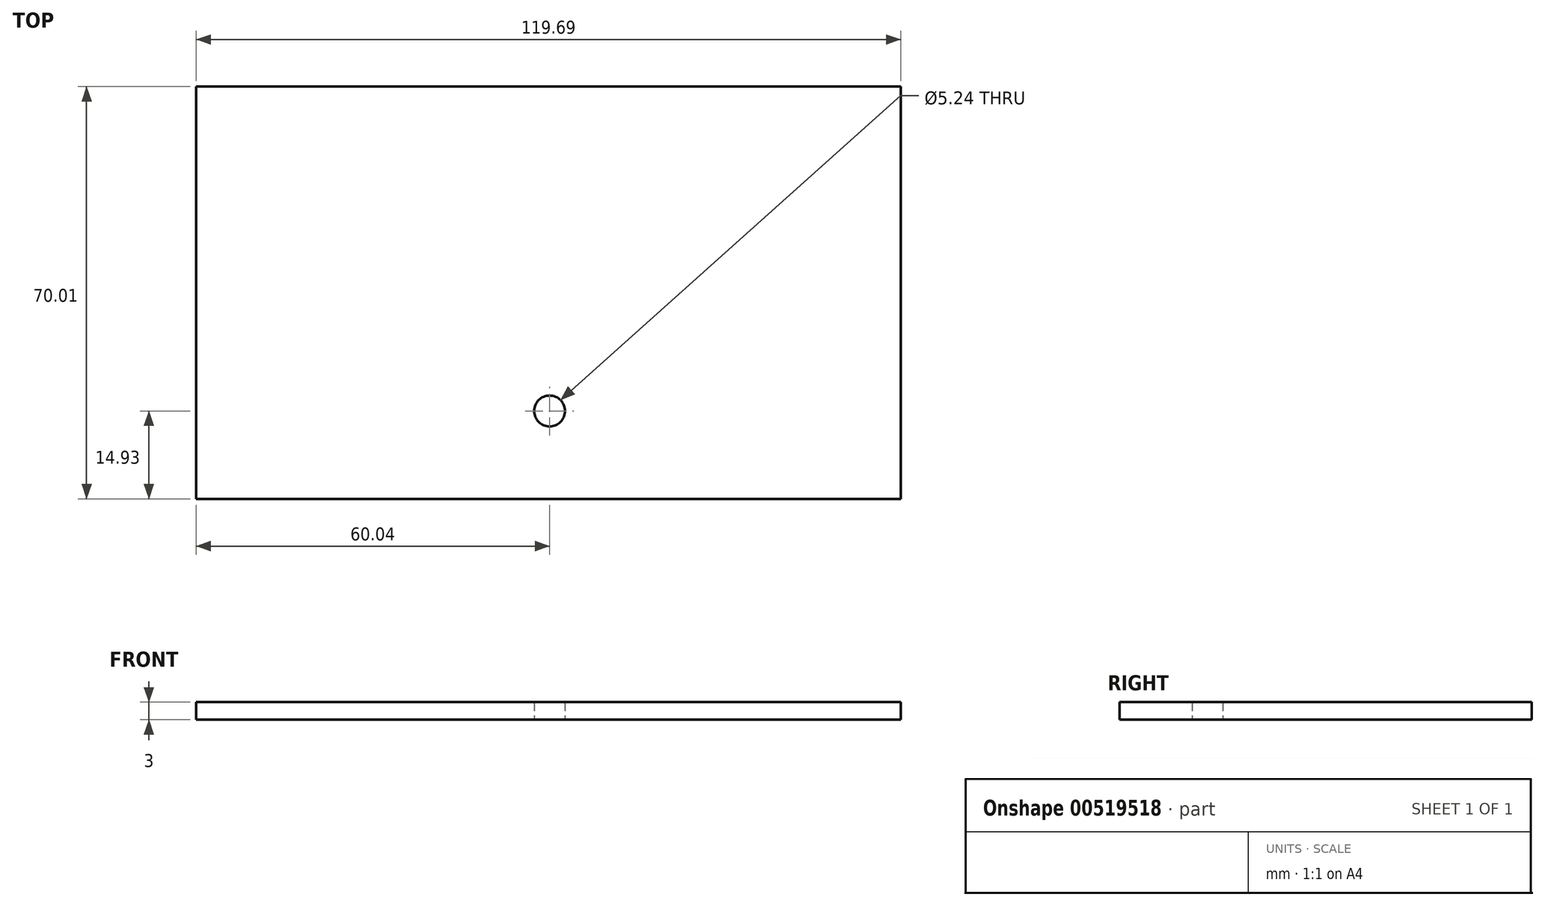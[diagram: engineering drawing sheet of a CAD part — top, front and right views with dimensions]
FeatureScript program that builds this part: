
annotation { "Feature Type Name" : "Feature", "Feature Type Description" : "" }
export const myFeature = defineFeature(function(context is Context, id is Id, definition is map)
    precondition{}
    {
        {
            var Q0;
            Q0=qCreatedBy(makeId("Top.planeOp"),FACE);
            var sketch = newSketch(context, id + "F0", { "sketchPlane" : qUnion([Q0])});
            skCircle(sketch, "E0", {"center": v(0, 0) * mm, "radius": 2.62 * mm});
            skLineSegment(sketch, "E1", {"start": v(0, -14.93) * mm, "end": v(59.65, -14.93) * mm});
            skLineSegment(sketch, "E2", {"start": v(59.65, -14.93) * mm, "end": v(59.65, 55.08) * mm});
            skLineSegment(sketch, "E3", {"start": v(59.65, 55.08) * mm, "end": v(-60.04, 55.08) * mm});
            skLineSegment(sketch, "E4", {"start": v(-60.04, 55.08) * mm, "end": v(-60.04, -14.93) * mm});
            skLineSegment(sketch, "E5", {"start": v(-60.04, -14.93) * mm, "end": v(0, -14.93) * mm});
            skSolve(sketch);
        }
        {
            var Q0;
            Q0=makeQuery(id+"F0.imprint","IMPRINT",FACE,{"disambiguationData":[TD([[makeQuery(id+"F0.imprint","IMPRINT",EDGE,{"derivedFrom":sQuery(id+"F0.wireOp",EDGE,"E0")}),-1.0]])]});
            extrude(context, id + "F1", {"entities" : qUnion([Q0]), "depth" : 3 * mm, "offsetDistance" : 25 * mm});
        }
    });
